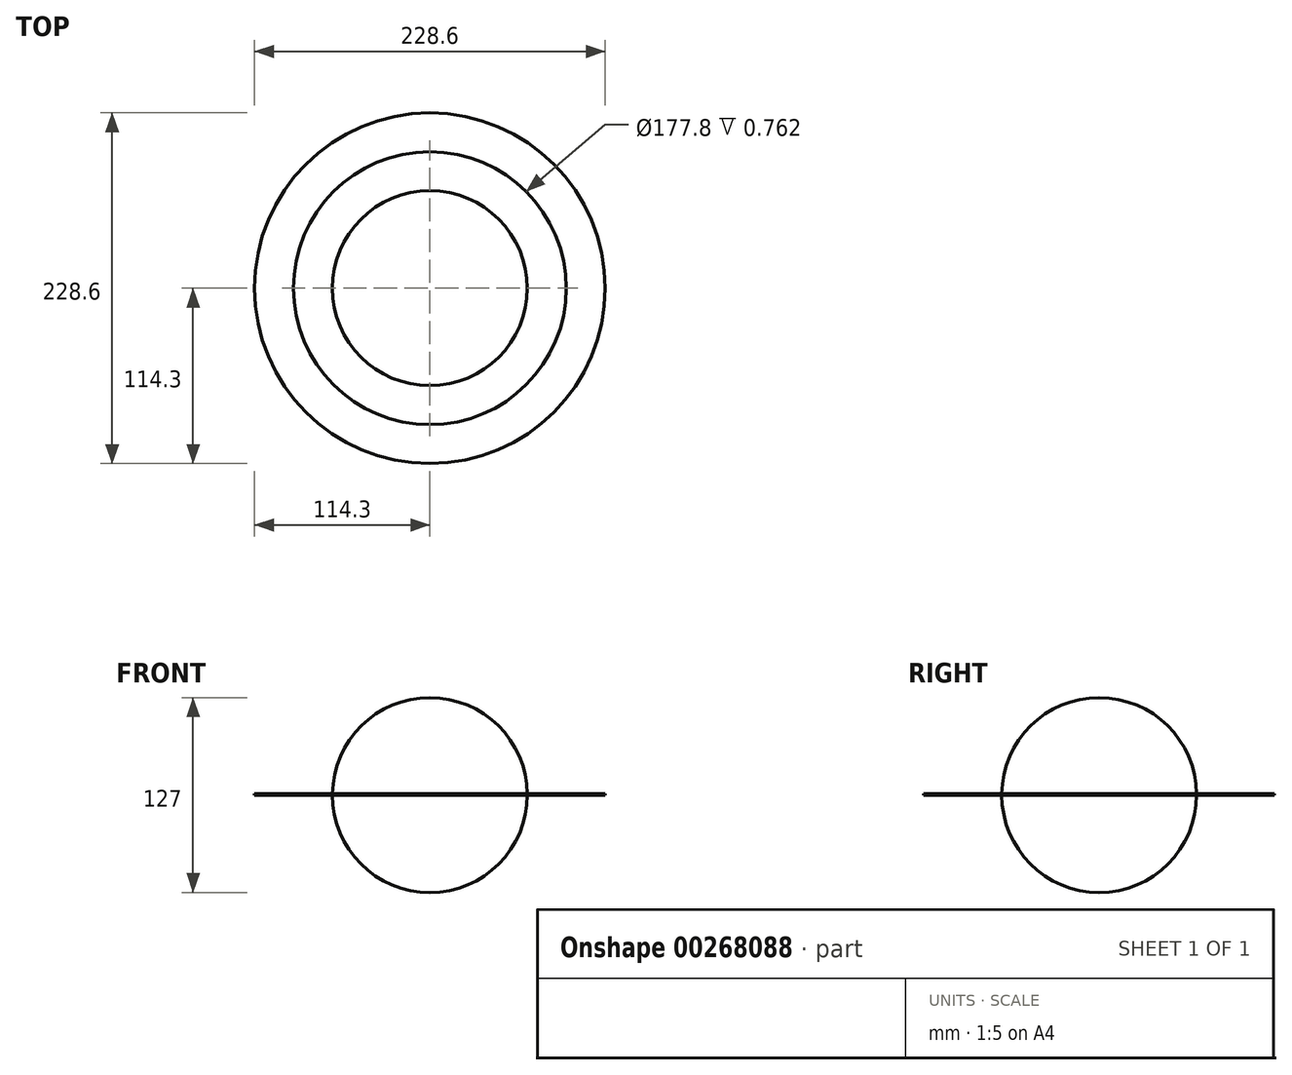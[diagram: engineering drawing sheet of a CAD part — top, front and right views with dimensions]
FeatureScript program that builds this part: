
annotation { "Feature Type Name" : "Feature", "Feature Type Description" : "" }
export const myFeature = defineFeature(function(context is Context, id is Id, definition is map)
    precondition{}
    {
        {
            var Q0;
            Q0=qCreatedBy(makeId("Top.planeOp"),FACE);
            var sketch = newSketch(context, id + "F0", { "sketchPlane" : qUnion([Q0])});
            skCircle(sketch, "E0", {"center": v(0, 0) * mm, "radius": 63.5 * mm});
            skSolve(sketch);
        }
        {
            var Q0;
            Q0=makeQuery(id+"F0.imprint","IMPRINT",FACE,{"disambiguationData":[TD([[makeQuery(id+"F0.imprint","IMPRINT",EDGE,{"derivedFrom":sQuery(id+"F0.wireOp",EDGE,"E0")}),1.0]])]});
            extrude(context, id + "F1", {"entities" : qUnion([Q0]), "depth" : 63.5 * mm});
        }
        {
            var Q0;
            Q0=makeQuery(id+"F1.opExtrude","CAP_FACE",FACE,{"disambiguationData":[OSD([sQuery(id+"F0.wireOp",EDGE,"E0")])],"isStart":true});
            extrude(context, id + "F2", {"entities" : qUnion([Q0]), "operationType" : NewBodyOperationType.ADD, "depth" : 63.5 * mm});
        }
        {
            var Q0;
            {var subQ0=sQuery(id+"F0.wireOp",EDGE,"E0");Q0=makeQuery(id+"F2.boolean.opBoolean","MERGE",FACE,{"derivedFrom":[makeQuery(id+"F1.opExtrude","SWEPT_FACE",FACE,{"disambiguationData":[OSD([subQ0])]}),makeQuery(id+"F2.opExtrude","SWEPT_FACE",FACE,{"disambiguationData":[OSD([subQ0])]})]});}
            fillet(context, id + "F3", {"entities" : qUnion([Q0]), "radius" : 63.5 * mm, "tangentPropagation" : true, "allowEdgeOverflow" : false});
        }
        {
            var Q0;
            Q0=qCreatedBy(makeId("Top.planeOp"),FACE);
            var sketch = newSketch(context, id + "F4", { "sketchPlane" : qUnion([Q0])});
            skCircle(sketch, "E1", {"center": v(0, 0) * mm, "radius": 88.9 * mm});
            skCircle(sketch, "E2", {"center": v(0, 0) * mm, "radius": 114.3 * mm});
            skSolve(sketch);
        }
        {
            var Q0;
            Q0=makeQuery(id+"F4.imprint","IMPRINT",FACE,{"disambiguationData":[TD([[makeQuery(id+"F4.imprint","IMPRINT",EDGE,{"derivedFrom":sQuery(id+"F4.wireOp",EDGE,"E1")}),-1.0]])]});
            extrude(context, id + "F5", {"entities" : qUnion([Q0]), "depth" : 0.76 * mm});
        }
    });
